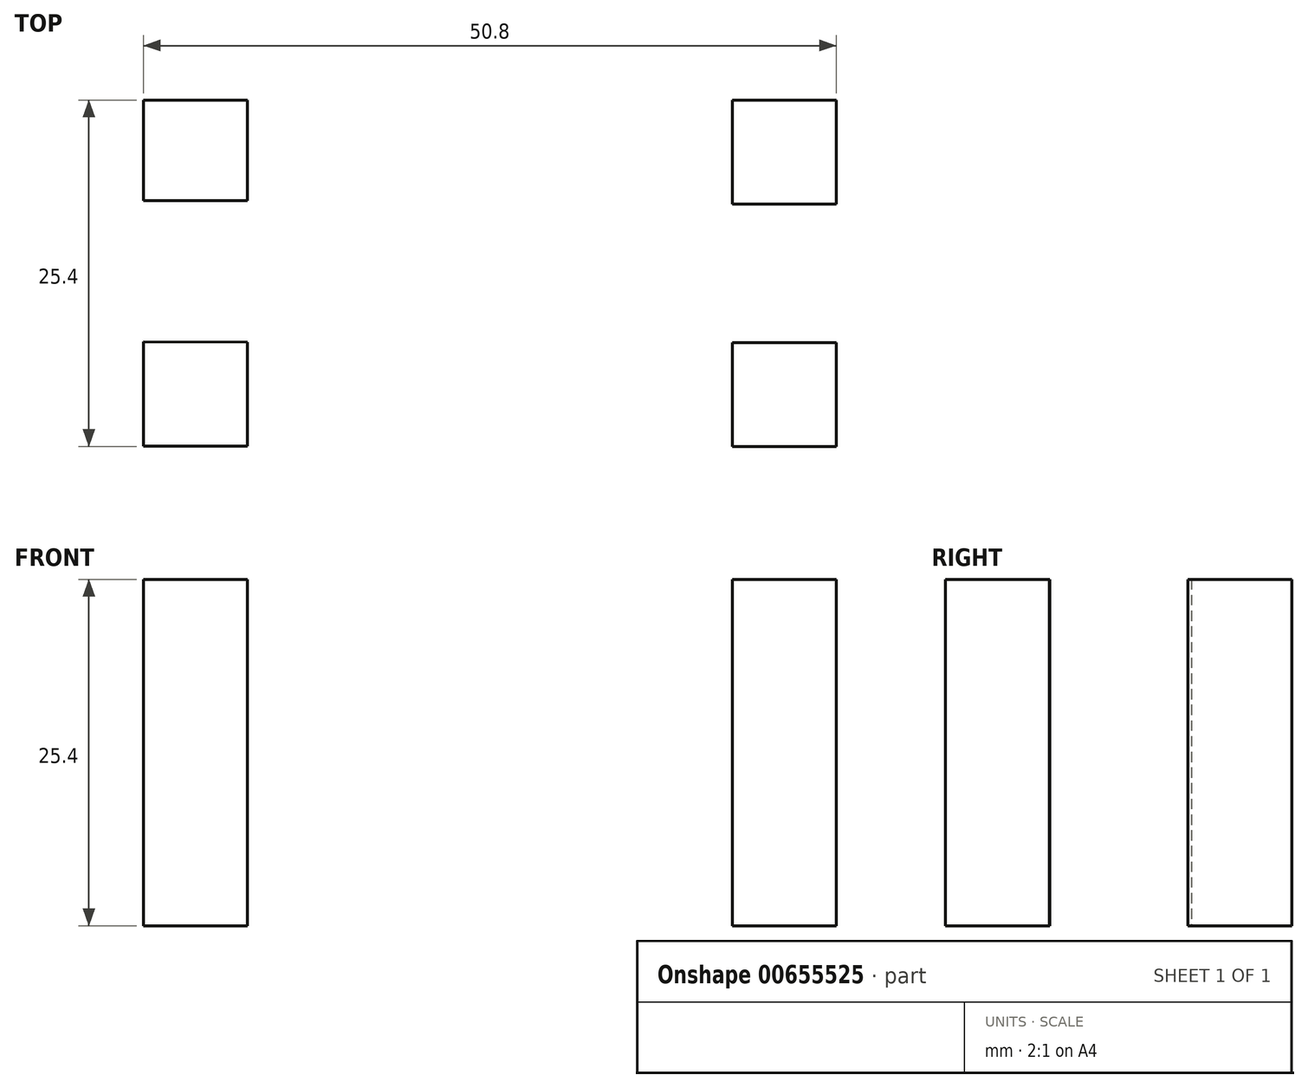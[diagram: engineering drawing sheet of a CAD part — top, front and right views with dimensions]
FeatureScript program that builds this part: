
annotation { "Feature Type Name" : "Feature", "Feature Type Description" : "" }
export const myFeature = defineFeature(function(context is Context, id is Id, definition is map)
    precondition{}
    {
        {
            var Q0;
            Q0=qCreatedBy(makeId("Top.planeOp"),FACE);
            var sketch = newSketch(context, id + "F0", { "sketchPlane" : qUnion([Q0])});
            skLineSegment(sketch, "E0.right", {"start": v(-17.78, -12.69) * mm, "end": v(-17.78, -5.07) * mm});
            skLineSegment(sketch, "E1", {"start": v(-17.78, -12.69) * mm, "end": v(-25.4, -12.69) * mm});
            skLineSegment(sketch, "E2", {"start": v(-25.4, -12.69) * mm, "end": v(-25.4, -5.04) * mm});
            skLineSegment(sketch, "E3", {"start": v(-25.4, -5.04) * mm, "end": v(-17.78, -5.07) * mm});
            skLineSegment(sketch, "E4.bottom", {"start": v(-25.4, 12.7) * mm, "end": v(-17.78, 12.7) * mm});
            skLineSegment(sketch, "E4.top", {"start": v(-25.4, 5.32) * mm, "end": v(-17.78, 5.32) * mm});
            skLineSegment(sketch, "E4.left", {"start": v(-25.4, 12.7) * mm, "end": v(-25.4, 5.32) * mm});
            skLineSegment(sketch, "E4.right", {"start": v(-17.78, 12.7) * mm, "end": v(-17.78, 5.32) * mm});
            skLineSegment(sketch, "E5.bottom", {"start": v(25.4, 12.7) * mm, "end": v(17.78, 12.7) * mm});
            skLineSegment(sketch, "E5.top", {"start": v(25.4, 5.08) * mm, "end": v(17.78, 5.08) * mm});
            skLineSegment(sketch, "E5.left", {"start": v(25.4, 12.7) * mm, "end": v(25.4, 5.08) * mm});
            skLineSegment(sketch, "E5.right", {"start": v(17.78, 12.7) * mm, "end": v(17.78, 5.08) * mm});
            skLineSegment(sketch, "E6.bottom", {"start": v(25.4, -12.7) * mm, "end": v(17.78, -12.7) * mm});
            skLineSegment(sketch, "E6.top", {"start": v(25.4, -5.08) * mm, "end": v(17.78, -5.08) * mm});
            skLineSegment(sketch, "E6.left", {"start": v(25.4, -12.7) * mm, "end": v(25.4, -5.08) * mm});
            skLineSegment(sketch, "E6.right", {"start": v(17.78, -12.7) * mm, "end": v(17.78, -5.08) * mm});
            skSolve(sketch);
        }
        {
            var Q0;
            Q0=qSketchRegion(id+"F0",true);
            extrude(context, id + "F1", {"entities" : qUnion([Q0]), "depth" : 25.4 * mm, "offsetDistance" : 25.4 * mm});
        }
    });
